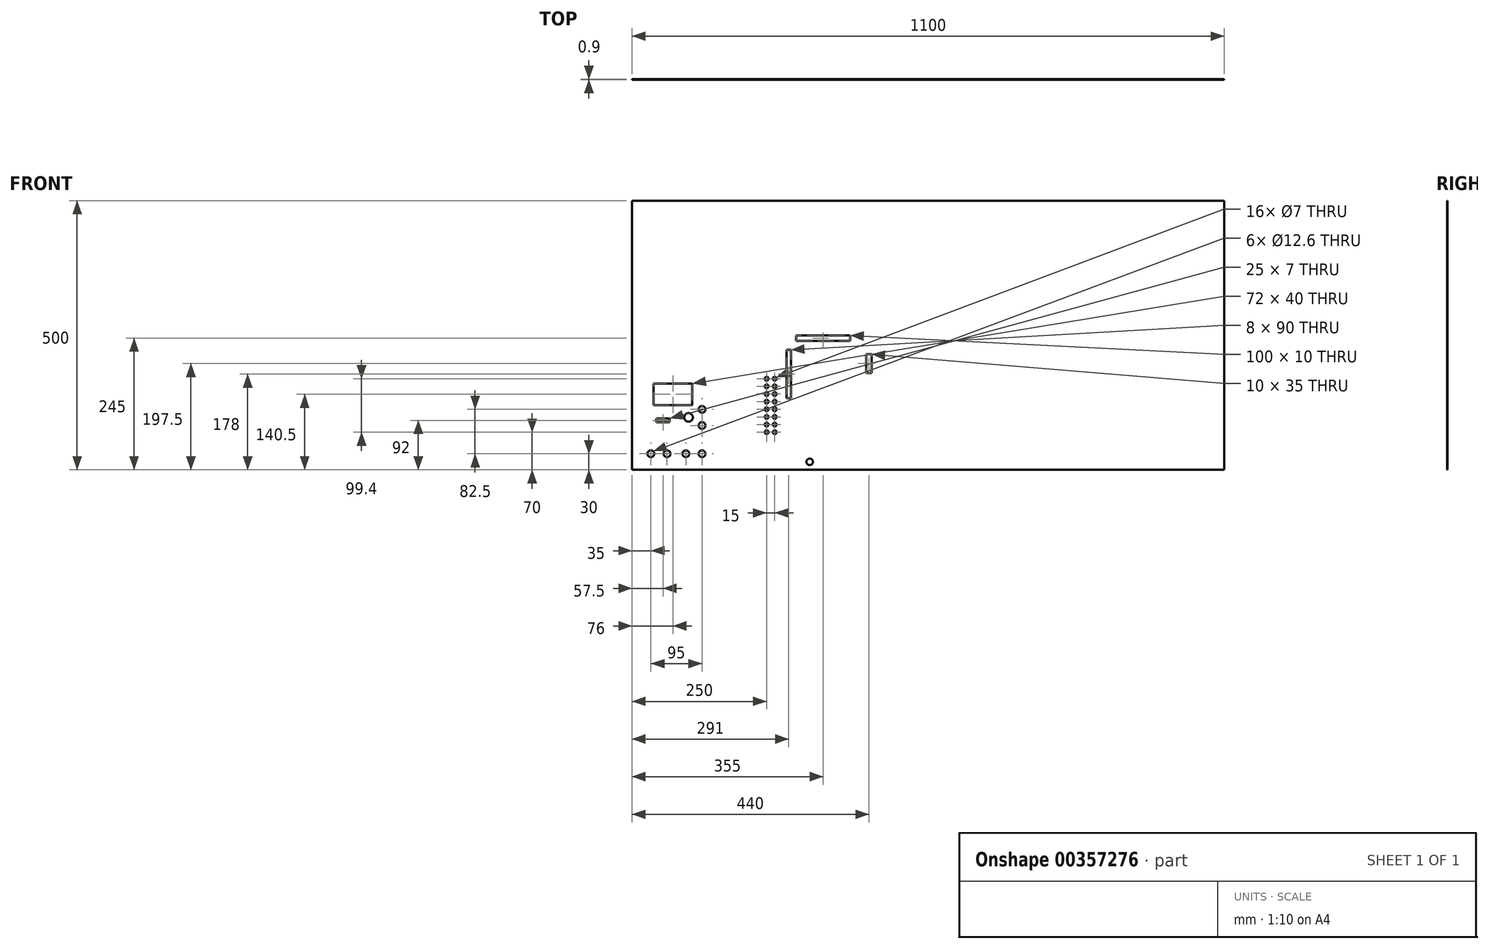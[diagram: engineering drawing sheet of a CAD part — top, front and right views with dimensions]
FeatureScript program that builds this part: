
annotation { "Feature Type Name" : "Feature", "Feature Type Description" : "" }
export const myFeature = defineFeature(function(context is Context, id is Id, definition is map)
    precondition{}
    {
        {
            var Q0;
            Q0=qCreatedBy(makeId("Front.planeOp"),FACE);
            var sketch = newSketch(context, id + "F0", { "sketchPlane" : qUnion([Q0])});
            skLineSegment(sketch, "E0.bottom", {"start": v(-550, -250) * mm, "end": v(550, -250) * mm});
            skLineSegment(sketch, "E0.top", {"start": v(-550, 250) * mm, "end": v(550, 250) * mm});
            skLineSegment(sketch, "E0.left", {"start": v(-550, -250) * mm, "end": v(-550, 250) * mm});
            skLineSegment(sketch, "E0.right", {"start": v(550, -250) * mm, "end": v(550, 250) * mm});
            skPoint(sketch, "E0.middle", {"position": v(0, 0) * mm});
            skCircle(sketch, "E1", {"center": v(-515, -220) * mm, "radius": 6.3 * mm});
            skCircle(sketch, "E2", {"center": v(-485, -220) * mm, "radius": 6.3 * mm});
            skCircle(sketch, "E3", {"center": v(-450, -220) * mm, "radius": 6.3 * mm});
            skCircle(sketch, "E4", {"center": v(-420, -220) * mm, "radius": 6.3 * mm});
            skLineSegment(sketch, "E5.bottom", {"start": v(-505, -154.5) * mm, "end": v(-480, -154.5) * mm});
            skLineSegment(sketch, "E5.top", {"start": v(-505, -161.5) * mm, "end": v(-480, -161.5) * mm});
            skLineSegment(sketch, "E5.left", {"start": v(-505, -154.5) * mm, "end": v(-505, -161.5) * mm});
            skLineSegment(sketch, "E5.right", {"start": v(-480, -154.5) * mm, "end": v(-480, -161.5) * mm});
            skLineSegment(sketch, "E6.bottom", {"start": v(-510, -89.5) * mm, "end": v(-438, -89.5) * mm});
            skLineSegment(sketch, "E6.top", {"start": v(-510, -129.5) * mm, "end": v(-438, -129.5) * mm});
            skLineSegment(sketch, "E6.left", {"start": v(-510, -89.5) * mm, "end": v(-510, -129.5) * mm});
            skLineSegment(sketch, "E6.right", {"start": v(-438, -89.5) * mm, "end": v(-438, -129.5) * mm});
            skCircle(sketch, "E7", {"center": v(-445, -152.5) * mm, "radius": 8 * mm});
            skCircle(sketch, "E8", {"center": v(-420, -137.5) * mm, "radius": 6.3 * mm});
            skCircle(sketch, "E9", {"center": v(-420, -167.5) * mm, "radius": 6.3 * mm});
            skLineSegment(sketch, "E10.bottom", {"start": v(-527.78, -232.5) * mm, "end": v(-407.78, -232.5) * mm, "construction": true});
            skLineSegment(sketch, "E10.top", {"start": v(-527.78, -207.5) * mm, "end": v(-407.78, -207.5) * mm, "construction": true});
            skLineSegment(sketch, "E10.left", {"start": v(-527.78, -232.5) * mm, "end": v(-527.78, -207.5) * mm, "construction": true});
            skLineSegment(sketch, "E10.right", {"start": v(-407.78, -232.5) * mm, "end": v(-407.78, -207.5) * mm, "construction": true});
            skPoint(sketch, "E10.middle", {"position": v(-467.78, -220) * mm});
            skLineSegment(sketch, "E11", {"start": v(-467.78, -207.5) * mm, "end": v(-467.78, -232.5) * mm, "construction": true});
            skLineSegment(sketch, "E12.bottom", {"start": v(-525, -77.5) * mm, "end": v(-405, -77.5) * mm, "construction": true});
            skLineSegment(sketch, "E12.top", {"start": v(-525, -177.5) * mm, "end": v(-405, -177.5) * mm, "construction": true});
            skLineSegment(sketch, "E12.left", {"start": v(-525, -77.5) * mm, "end": v(-525, -177.5) * mm, "construction": true});
            skLineSegment(sketch, "E12.right", {"start": v(-405, -77.5) * mm, "end": v(-405, -177.5) * mm, "construction": true});
            skCircle(sketch, "E13", {"center": v(-300, -180) * mm, "radius": 3.5 * mm});
            skCircle(sketch, "E14.0.1.0", {"center": v(-300, -165.8) * mm, "radius": 3.5 * mm});
            skCircle(sketch, "E14.0.2.0", {"center": v(-300, -151.6) * mm, "radius": 3.5 * mm});
            skCircle(sketch, "E14.0.3.0", {"center": v(-300, -137.4) * mm, "radius": 3.5 * mm});
            skCircle(sketch, "E14.0.4.0", {"center": v(-300, -123.2) * mm, "radius": 3.5 * mm});
            skCircle(sketch, "E14.0.5.0", {"center": v(-300, -109) * mm, "radius": 3.5 * mm});
            skCircle(sketch, "E14.0.6.0", {"center": v(-300, -94.8) * mm, "radius": 3.5 * mm});
            skCircle(sketch, "E14.0.7.0", {"center": v(-300, -80.6) * mm, "radius": 3.5 * mm});
            skCircle(sketch, "E14.1.0.0", {"center": v(-285, -180) * mm, "radius": 3.5 * mm});
            skCircle(sketch, "E14.1.1.0", {"center": v(-285, -165.8) * mm, "radius": 3.5 * mm});
            skCircle(sketch, "E14.1.2.0", {"center": v(-285, -151.6) * mm, "radius": 3.5 * mm});
            skCircle(sketch, "E14.1.3.0", {"center": v(-285, -137.4) * mm, "radius": 3.5 * mm});
            skCircle(sketch, "E14.1.4.0", {"center": v(-285, -123.2) * mm, "radius": 3.5 * mm});
            skCircle(sketch, "E14.1.5.0", {"center": v(-285, -109) * mm, "radius": 3.5 * mm});
            skCircle(sketch, "E14.1.6.0", {"center": v(-285, -94.8) * mm, "radius": 3.5 * mm});
            skCircle(sketch, "E14.1.7.0", {"center": v(-285, -80.6) * mm, "radius": 3.5 * mm});
            skLineSegment(sketch, "E14.direction1", {"start": v(-300, -180) * mm, "end": v(-285, -180) * mm, "construction": true});
            skLineSegment(sketch, "E14.direction2", {"start": v(-300, -180) * mm, "end": v(-300, -165.8) * mm, "construction": true});
            skLineSegment(sketch, "E15.bottom", {"start": v(-310, -70.6) * mm, "end": v(-275, -70.6) * mm, "construction": true});
            skLineSegment(sketch, "E15.top", {"start": v(-310, -190) * mm, "end": v(-275, -190) * mm, "construction": true});
            skLineSegment(sketch, "E15.left", {"start": v(-310, -70.6) * mm, "end": v(-310, -190) * mm, "construction": true});
            skLineSegment(sketch, "E15.right", {"start": v(-275, -70.6) * mm, "end": v(-275, -190) * mm, "construction": true});
            skSolve(sketch);
        }
        {
            var Q0;
            Q0=makeQuery(id+"F0.imprint","IMPRINT",FACE,{"disambiguationData":[TD([[makeQuery(id+"F0.imprint","IMPRINT",EDGE,{"derivedFrom":sQuery(id+"F0.wireOp",EDGE,"E0.bottom")}),1.0]])]});
            extrude(context, id + "F1", {"entities" : qUnion([Q0]), "endBound" : BoundingType.SYMMETRIC, "depth" : 0.9 * mm});
        }
        {
            var Q0;
            Q0=makeQuery(id+"F1.opExtrude","CAP_FACE",FACE,{"disambiguationData":[OSD([sQuery(id+"F0.wireOp",EDGE,"E0.bottom"),sQuery(id+"F0.wireOp",EDGE,"E0.top"),sQuery(id+"F0.wireOp",EDGE,"E0.left"),sQuery(id+"F0.wireOp",EDGE,"E0.right"),sQuery(id+"F0.wireOp",EDGE,"E1"),sQuery(id+"F0.wireOp",EDGE,"E2"),sQuery(id+"F0.wireOp",EDGE,"E3"),sQuery(id+"F0.wireOp",EDGE,"E4"),sQuery(id+"F0.wireOp",EDGE,"E5.bottom"),sQuery(id+"F0.wireOp",EDGE,"E5.top"),sQuery(id+"F0.wireOp",EDGE,"E5.left"),sQuery(id+"F0.wireOp",EDGE,"E5.right"),sQuery(id+"F0.wireOp",EDGE,"E6.bottom"),sQuery(id+"F0.wireOp",EDGE,"E6.top"),sQuery(id+"F0.wireOp",EDGE,"E6.left"),sQuery(id+"F0.wireOp",EDGE,"E6.right"),sQuery(id+"F0.wireOp",EDGE,"E7"),sQuery(id+"F0.wireOp",EDGE,"E8"),sQuery(id+"F0.wireOp",EDGE,"E9"),sQuery(id+"F0.wireOp",EDGE,"E13"),sQuery(id+"F0.wireOp",EDGE,"E14.0.1.0"),sQuery(id+"F0.wireOp",EDGE,"E14.0.2.0"),sQuery(id+"F0.wireOp",EDGE,"E14.0.3.0"),sQuery(id+"F0.wireOp",EDGE,"E14.0.4.0"),sQuery(id+"F0.wireOp",EDGE,"E14.0.5.0"),sQuery(id+"F0.wireOp",EDGE,"E14.0.6.0"),sQuery(id+"F0.wireOp",EDGE,"E14.0.7.0"),sQuery(id+"F0.wireOp",EDGE,"E14.1.0.0"),sQuery(id+"F0.wireOp",EDGE,"E14.1.1.0"),sQuery(id+"F0.wireOp",EDGE,"E14.1.2.0"),sQuery(id+"F0.wireOp",EDGE,"E14.1.3.0"),sQuery(id+"F0.wireOp",EDGE,"E14.1.4.0"),sQuery(id+"F0.wireOp",EDGE,"E14.1.5.0"),sQuery(id+"F0.wireOp",EDGE,"E14.1.6.0"),sQuery(id+"F0.wireOp",EDGE,"E14.1.7.0")])],"isStart":false});
            var sketch = newSketch(context, id + "F2", { "sketchPlane" : qUnion([Q0])});
            skCircle(sketch, "E16", {"center": v(-220, -235) * mm, "radius": 6 * mm});
            skLineSegment(sketch, "E17.bottom", {"start": v(-115, -35) * mm, "end": v(-105, -35) * mm});
            skLineSegment(sketch, "E17.top", {"start": v(-115, -70) * mm, "end": v(-105, -70) * mm});
            skLineSegment(sketch, "E17.left", {"start": v(-115, -35) * mm, "end": v(-115, -70) * mm});
            skLineSegment(sketch, "E17.right", {"start": v(-105, -35) * mm, "end": v(-105, -70) * mm});
            skLineSegment(sketch, "E18.bottom", {"start": v(-245, 0) * mm, "end": v(-145, 0) * mm});
            skLineSegment(sketch, "E18.top", {"start": v(-245, -10) * mm, "end": v(-145, -10) * mm});
            skLineSegment(sketch, "E18.left", {"start": v(-245, 0) * mm, "end": v(-245, -10) * mm});
            skLineSegment(sketch, "E18.right", {"start": v(-145, 0) * mm, "end": v(-145, -10) * mm});
            skLineSegment(sketch, "E19.bottom", {"start": v(-255, -27) * mm, "end": v(-263, -27) * mm});
            skLineSegment(sketch, "E19.top", {"start": v(-255, -117) * mm, "end": v(-263, -117) * mm});
            skLineSegment(sketch, "E19.left", {"start": v(-255, -27) * mm, "end": v(-255, -117) * mm});
            skLineSegment(sketch, "E19.right", {"start": v(-263, -27) * mm, "end": v(-263, -117) * mm});
            skSolve(sketch);
        }
        {
            var Q0;
            Q0 = qSketchRegion(id + "F2", true);
            extrude(context, id + "F3", {"entities" : qUnion([Q0]), "operationType" : NewBodyOperationType.REMOVE, "endBound" : BoundingType.SYMMETRIC, "oppositeDirection" : true, "depth" : 25 * mm});
        }
    });
